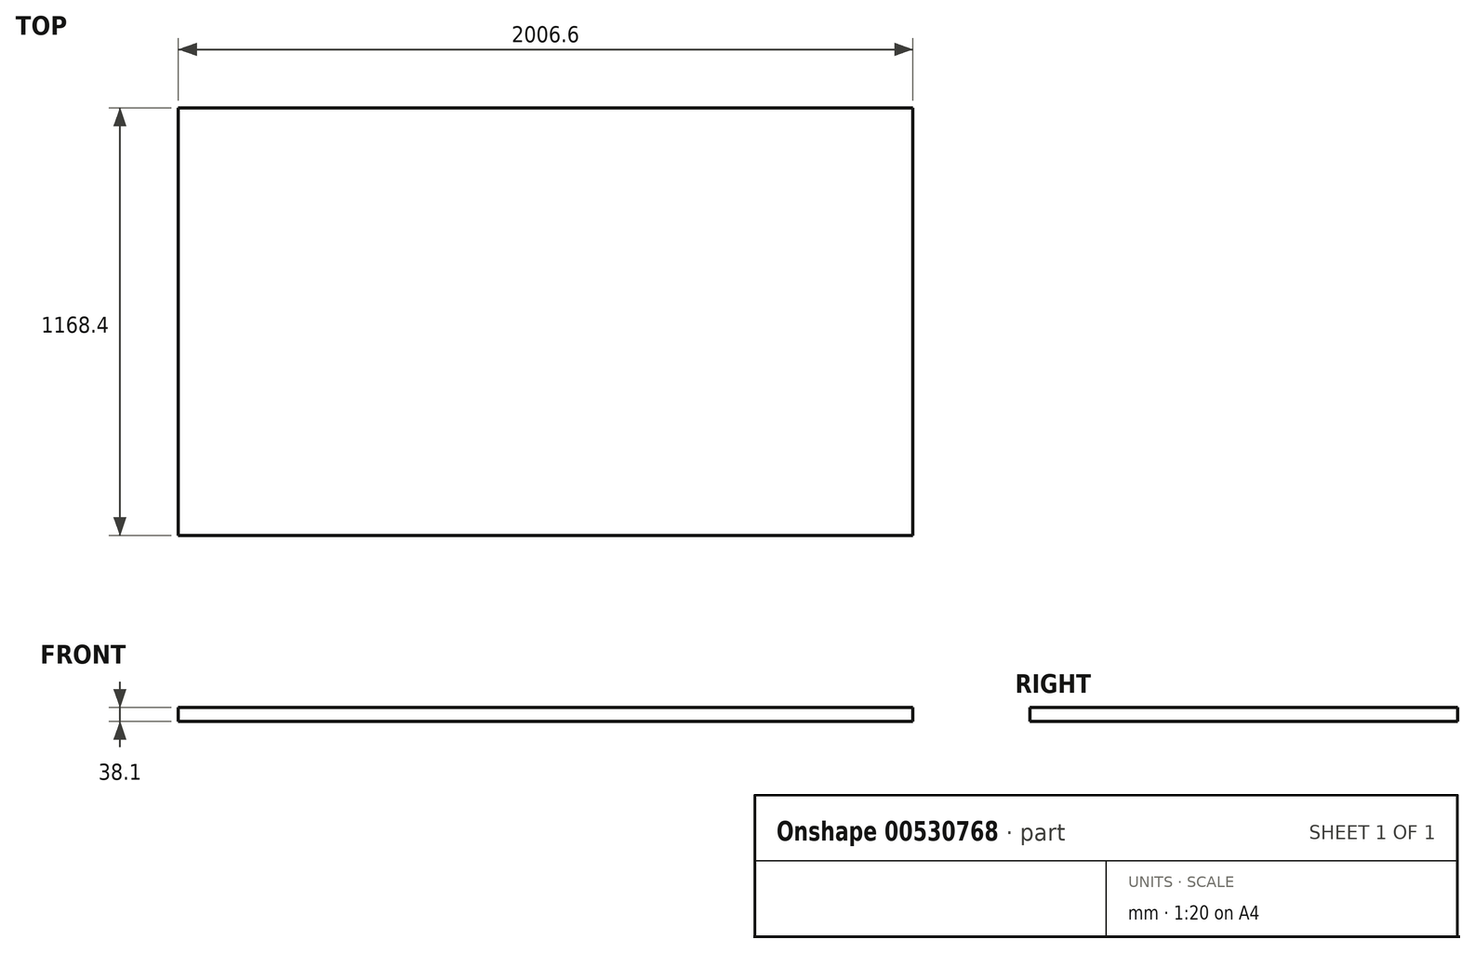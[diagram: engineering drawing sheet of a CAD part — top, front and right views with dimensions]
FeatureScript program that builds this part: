
annotation { "Feature Type Name" : "Feature", "Feature Type Description" : "" }
export const myFeature = defineFeature(function(context is Context, id is Id, definition is map)
    precondition{}
    {
        {
            var Q0;
            Q0=qCreatedBy(makeId("Top.planeOp"),FACE);
            var sketch = newSketch(context, id + "F0", { "sketchPlane" : qUnion([Q0])});
            skLineSegment(sketch, "E0", {"start": v(0, 0) * mm, "end": v(-2006.6, 0) * mm});
            skLineSegment(sketch, "E1", {"start": v(-2006.6, 0) * mm, "end": v(-2006.6, -1168.4) * mm});
            skLineSegment(sketch, "E2", {"start": v(-2006.6, -1168.4) * mm, "end": v(0, -1168.4) * mm});
            skLineSegment(sketch, "E3", {"start": v(0, -1168.4) * mm, "end": v(0, 0) * mm});
            skSolve(sketch);
        }
        {
            var Q0;
            Q0 = qSketchRegion(id + "F0", true);
            extrude(context, id + "F1", {"entities" : qUnion([Q0]), "depth" : 38.1 * mm, "offsetDistance" : 25.4 * mm});
        }
    });
